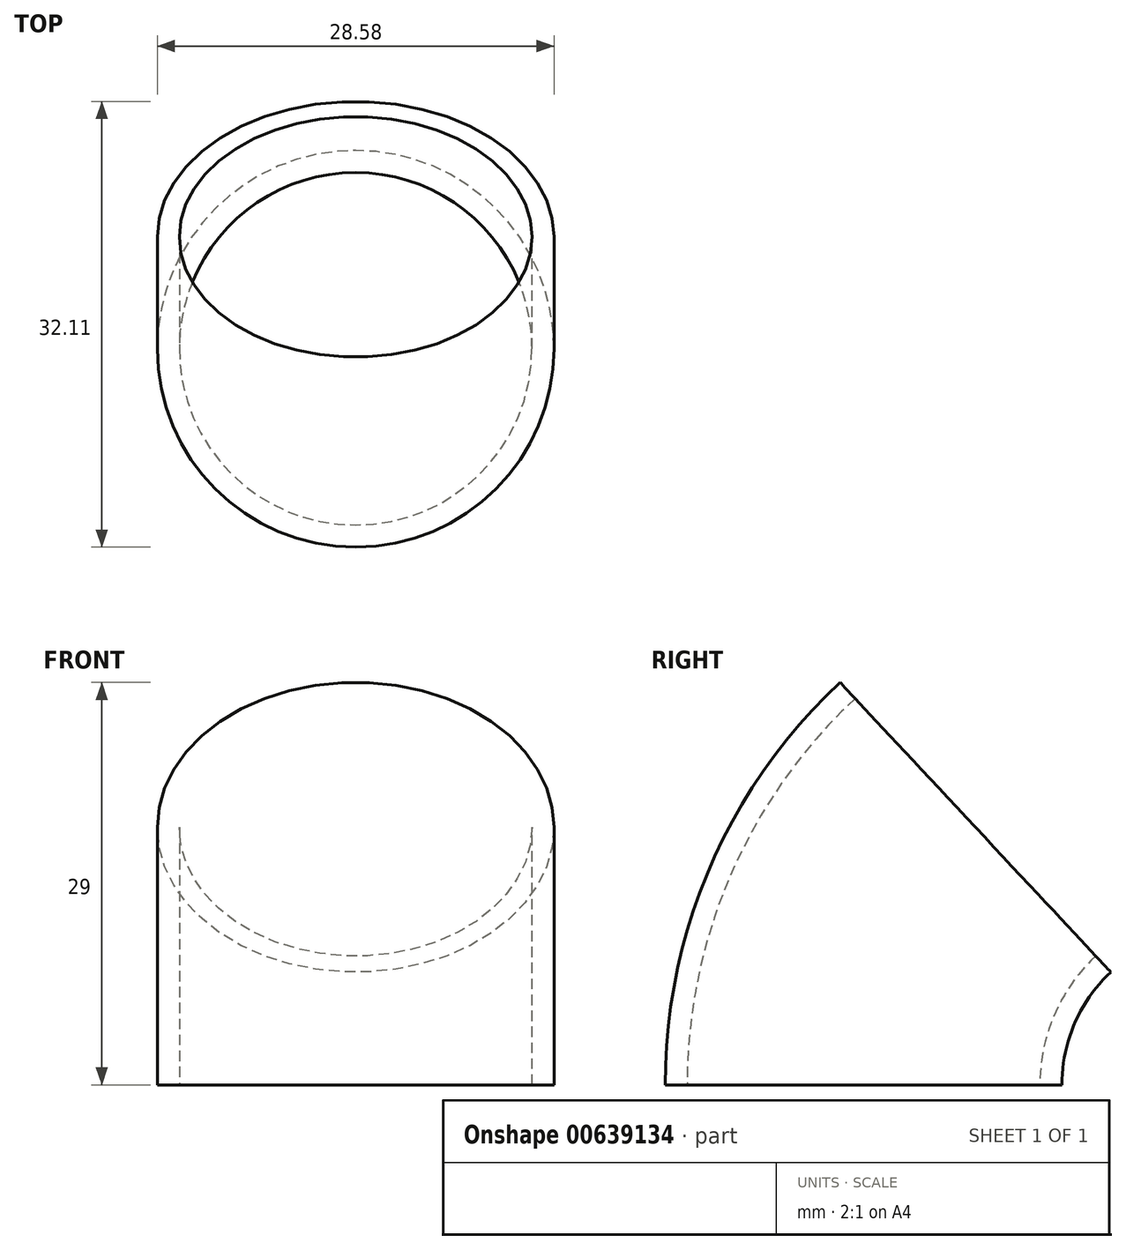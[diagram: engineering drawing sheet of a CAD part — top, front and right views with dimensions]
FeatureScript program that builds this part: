
annotation { "Feature Type Name" : "Feature", "Feature Type Description" : "" }
export const myFeature = defineFeature(function(context is Context, id is Id, definition is map)
    precondition{}
    {
        {
            var Q0;
            Q0=qCreatedBy(makeId("Top.planeOp"),FACE);
            var sketch = newSketch(context, id + "F0", { "sketchPlane" : qUnion([Q0])});
            skLineSegment(sketch, "E0", {"start": v(0, 0) * mm, "end": v(12.7, 0) * mm});
            skCircle(sketch, "E1", {"center": v(0, 0) * mm, "radius": 12.7 * mm});
            skCircle(sketch, "E2.0", {"center": v(0, 0) * mm, "radius": 14.29 * mm});
            skSolve(sketch);
        }
        {
            var Q0;
            Q0=qCreatedBy(makeId("Right.planeOp"),FACE);
            var sketch = newSketch(context, id + "F1", { "sketchPlane" : qUnion([Q0])});
            skLineSegment(sketch, "E3", {"start": v(0, 0) * mm, "end": v(0, 0) * mm});
            skLineSegment(sketch, "E4", {"start": v(0, 0) * mm, "end": v(25.4, 0) * mm});
            skArc(sketch, "E5", {"start": v(0, 0) * mm, "mid": v(2.1, 10.12) * mm, "end": v(8.06, 18.56) * mm});
            skLineSegment(sketch, "E6", {"start": v(0, 0) * mm, "end": v(0, 25.4) * mm});
            skArc(sketch, "E7", {"start": v(8.06, 18.56) * mm, "mid": v(16.08, 23.63) * mm, "end": v(25.4, 25.4) * mm});
            skLineSegment(sketch, "E8", {"start": v(8.06, 18.56) * mm, "end": v(25.4, 0) * mm});
            skSolve(sketch);
        }
        {
            var Q0;
            Q0=qSketchRegion(id+"F0",true);
            var Q1;
            Q1=sQuery(id+"F1.wireOp",EDGE,"E5");
            sweep(context, id + "F2", {"profiles" : qUnion([Q0]), "path" : qUnion([Q1])});
        }
    });
